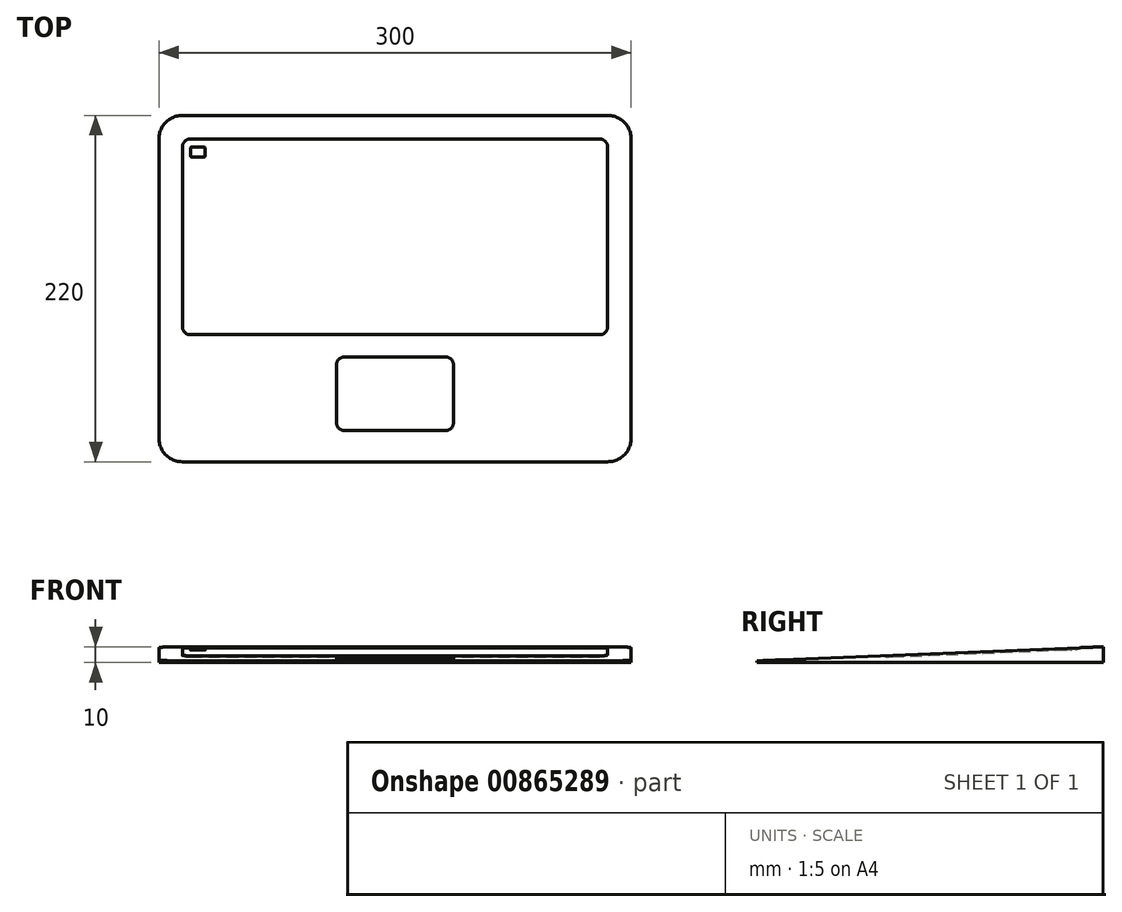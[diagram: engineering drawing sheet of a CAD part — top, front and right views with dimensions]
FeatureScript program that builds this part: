
annotation { "Feature Type Name" : "Feature", "Feature Type Description" : "" }
export const myFeature = defineFeature(function(context is Context, id is Id, definition is map)
    precondition{}
    {
        {
            var Q0;
            Q0=qCreatedBy(makeId("Right.planeOp"),FACE);
            var sketch = newSketch(context, id + "F0", { "sketchPlane" : qUnion([Q0])});
            skLineSegment(sketch, "E0", {"start": v(-104.21, 0) * mm, "end": v(115.79, 0) * mm});
            skLineSegment(sketch, "E1", {"start": v(115.79, 0) * mm, "end": v(115.79, 10) * mm});
            skLineSegment(sketch, "E2", {"start": v(115.79, 10) * mm, "end": v(-104.21, 1) * mm});
            skLineSegment(sketch, "E3", {"start": v(-104.21, 1) * mm, "end": v(-104.21, 0) * mm});
            skSolve(sketch);
        }
        {
            var Q0;
            Q0=makeQuery(id+"F0.imprint","IMPRINT",FACE,{"disambiguationData":[TD([[makeQuery(id+"F0.imprint","IMPRINT",EDGE,{"derivedFrom":sQuery(id+"F0.wireOp",EDGE,"E0")}),1.0]])]});
            extrude(context, id + "F1", {"entities" : qUnion([Q0]), "depth" : 300 * mm, "offsetDistance" : 25 * mm});
        }
        {
            var Q0;
            Q0=makeQuery(id+"F1.opExtrude","CAP_EDGE",EDGE,{"disambiguationData":[OSD([sQuery(id+"F0.wireOp",EDGE,"E1")])],"isStart":false});
            var Q1;
            Q1=makeQuery(id+"F1.opExtrude","CAP_EDGE",EDGE,{"disambiguationData":[OSD([sQuery(id+"F0.wireOp",EDGE,"E1")])],"isStart":true});
            var Q2;
            Q2=makeQuery(id+"F1.opExtrude","CAP_EDGE",EDGE,{"disambiguationData":[OSD([sQuery(id+"F0.wireOp",EDGE,"E3")])],"isStart":true});
            var Q3;
            Q3=makeQuery(id+"F1.opExtrude","CAP_EDGE",EDGE,{"disambiguationData":[OSD([sQuery(id+"F0.wireOp",EDGE,"E3")])],"isStart":false});
            fillet(context, id + "F2", {"entities" : qUnion([Q0, Q1, Q2, Q3]), "radius" : 15 * mm, "tangentPropagation" : true, "allowEdgeOverflow" : false});
        }
        {
            var Q0;
            Q0=makeQuery(id+"F1.opExtrude","SWEPT_FACE",FACE,{"disambiguationData":[OSD([sQuery(id+"F0.wireOp",EDGE,"E2")])]});
            var sketch = newSketch(context, id + "F3", { "sketchPlane" : qUnion([Q0])});
            skPoint(sketch, "E4.oppositeSnap0", {"position": v(285, 86.08) * mm});
            skLineSegment(sketch, "E4.bottom", {"start": v(20, 101.09) * mm, "end": v(280, 101.09) * mm});
            skLineSegment(sketch, "E4.top", {"start": v(20, -23.33) * mm, "end": v(280, -23.33) * mm});
            skLineSegment(sketch, "E4.left", {"start": v(15, 96.09) * mm, "end": v(15, -18.33) * mm});
            skLineSegment(sketch, "E4.right", {"start": v(285, 96.09) * mm, "end": v(285, -18.33) * mm});
            skPoint(sketch, "E5.visualSharp", {"position": v(15, 101.09) * mm});
            skArc(sketch, "E5.filletArc", {"start": v(20, 101.09) * mm, "mid": v(16.46, 99.62) * mm, "end": v(15, 96.09) * mm});
            skPoint(sketch, "E6.visualSharp", {"position": v(285, 101.09) * mm});
            skArc(sketch, "E6.filletArc", {"start": v(285, 96.09) * mm, "mid": v(283.54, 99.62) * mm, "end": v(280, 101.09) * mm});
            skPoint(sketch, "E7.visualSharp", {"position": v(285, -23.33) * mm});
            skArc(sketch, "E7.filletArc", {"start": v(280, -23.33) * mm, "mid": v(283.54, -21.86) * mm, "end": v(285, -18.33) * mm});
            skPoint(sketch, "E8.visualSharp", {"position": v(15, -23.33) * mm});
            skArc(sketch, "E8.filletArc", {"start": v(15, -18.33) * mm, "mid": v(16.46, -21.86) * mm, "end": v(20, -23.33) * mm});
            skSolve(sketch);
        }
        {
            var Q0;
            Q0=makeQuery(id+"F3.imprint","IMPRINT",FACE,{"disambiguationData":[TD([[makeQuery(id+"F3.imprint","IMPRINT",EDGE,{"derivedFrom":sQuery(id+"F3.wireOp",EDGE,"E4.bottom")}),-1.0]])]});
            extrude(context, id + "F4", {"entities" : qUnion([Q0]), "operationType" : NewBodyOperationType.REMOVE, "oppositeDirection" : true, "depth" : 1 * mm, "offsetDistance" : 25 * mm});
        }
        {
            var Q0;
            Q0=makeQuery(id+"F4.boolean.opBoolean","COPY",FACE,{"derivedFrom":makeQuery(id+"F4.opExtrude","CAP_FACE",FACE,{"disambiguationData":[OSD([sQuery(id+"F3.wireOp",EDGE,"E4.bottom"),sQuery(id+"F3.wireOp",EDGE,"E4.top"),sQuery(id+"F3.wireOp",EDGE,"E4.left"),sQuery(id+"F3.wireOp",EDGE,"E4.right")])],"isStart":false})});
            fillet(context, id + "F5", {"entities" : qUnion([Q0]), "radius" : 5 * mm, "tangentPropagation" : true, "allowEdgeOverflow" : false});
        }
        {
            var Q0;
            Q0=makeQuery(id+"F1.opExtrude","SWEPT_FACE",FACE,{"disambiguationData":[OSD([sQuery(id+"F0.wireOp",EDGE,"E2")])]});
            var sketch = newSketch(context, id + "F6", { "sketchPlane" : qUnion([Q0])});
            skLineSegment(sketch, "E9.bottom", {"start": v(117.9, -37.42) * mm, "end": v(182.1, -37.42) * mm});
            skLineSegment(sketch, "E9.top", {"start": v(117.9, -84.3) * mm, "end": v(182.1, -84.3) * mm});
            skLineSegment(sketch, "E9.left", {"start": v(112.9, -42.42) * mm, "end": v(112.9, -79.3) * mm});
            skLineSegment(sketch, "E9.right", {"start": v(187.1, -42.42) * mm, "end": v(187.1, -79.3) * mm});
            skPoint(sketch, "E9.middle", {"position": v(150, -60.85) * mm});
            skPoint(sketch, "E9.middle.positionSnap0", {"position": v(150, -23.33) * mm});
            skPoint(sketch, "E9.centerSnap0", {"position": v(150, -23.33) * mm});
            skPoint(sketch, "E10.visualSharp", {"position": v(112.9, -37.42) * mm});
            skArc(sketch, "E10.filletArc", {"start": v(117.9, -37.42) * mm, "mid": v(114.37, -38.88) * mm, "end": v(112.9, -42.42) * mm});
            skPoint(sketch, "E11.visualSharp", {"position": v(187.1, -37.42) * mm});
            skArc(sketch, "E11.filletArc", {"start": v(187.1, -42.42) * mm, "mid": v(185.63, -38.88) * mm, "end": v(182.1, -37.42) * mm});
            skPoint(sketch, "E12.visualSharp", {"position": v(187.1, -84.3) * mm});
            skArc(sketch, "E12.filletArc", {"start": v(182.1, -84.3) * mm, "mid": v(185.63, -82.83) * mm, "end": v(187.1, -79.3) * mm});
            skPoint(sketch, "E13.visualSharp", {"position": v(112.9, -84.3) * mm});
            skArc(sketch, "E13.filletArc", {"start": v(112.9, -79.3) * mm, "mid": v(114.37, -82.83) * mm, "end": v(117.9, -84.3) * mm});
            skSolve(sketch);
        }
        {
            var Q0;
            Q0=makeQuery(id+"F6.imprint","IMPRINT",FACE,{"disambiguationData":[TD([[makeQuery(id+"F6.imprint","IMPRINT",EDGE,{"derivedFrom":sQuery(id+"F6.wireOp",EDGE,"E9.bottom")}),-1.0]])]});
            extrude(context, id + "F7", {"entities" : qUnion([Q0]), "operationType" : NewBodyOperationType.REMOVE, "oppositeDirection" : true, "depth" : 0.1 * mm, "offsetDistance" : 25 * mm});
        }
        {
            var Q0;
            Q0=makeQuery(id+"F4.boolean.opBoolean","COPY",FACE,{"derivedFrom":makeQuery(id+"F4.opExtrude","CAP_FACE",FACE,{"disambiguationData":[OSD([sQuery(id+"F3.wireOp",EDGE,"E4.bottom"),sQuery(id+"F3.wireOp",EDGE,"E4.top"),sQuery(id+"F3.wireOp",EDGE,"E4.left"),sQuery(id+"F3.wireOp",EDGE,"E4.right"),sQuery(id+"F3.wireOp",EDGE,"E5.filletArc"),sQuery(id+"F3.wireOp",EDGE,"E6.filletArc"),sQuery(id+"F3.wireOp",EDGE,"E7.filletArc"),sQuery(id+"F3.wireOp",EDGE,"E8.filletArc")])],"isStart":false})});
            var sketch = newSketch(context, id + "F8", { "sketchPlane" : qUnion([Q0])});
            skLineSegment(sketch, "E14.bottom", {"start": v(21, 96.09) * mm, "end": v(28.5, 96.09) * mm});
            skLineSegment(sketch, "E14.top", {"start": v(21, 89.47) * mm, "end": v(28.5, 89.47) * mm});
            skLineSegment(sketch, "E14.left", {"start": v(20, 95.09) * mm, "end": v(20, 90.47) * mm});
            skLineSegment(sketch, "E14.right", {"start": v(29.5, 95.09) * mm, "end": v(29.5, 90.47) * mm});
            skPoint(sketch, "E15.visualSharp", {"position": v(20, 96.09) * mm});
            skArc(sketch, "E15.filletArc", {"start": v(21, 96.09) * mm, "mid": v(20.3, 95.8) * mm, "end": v(20, 95.09) * mm});
            skPoint(sketch, "E16.visualSharp", {"position": v(29.5, 96.09) * mm});
            skArc(sketch, "E16.filletArc", {"start": v(29.5, 95.09) * mm, "mid": v(29.21, 95.8) * mm, "end": v(28.5, 96.09) * mm});
            skPoint(sketch, "E17.visualSharp", {"position": v(29.5, 89.47) * mm});
            skArc(sketch, "E17.filletArc", {"start": v(28.5, 89.47) * mm, "mid": v(29.21, 89.77) * mm, "end": v(29.5, 90.47) * mm});
            skPoint(sketch, "E18.visualSharp", {"position": v(20, 89.47) * mm});
            skArc(sketch, "E18.filletArc", {"start": v(20, 90.47) * mm, "mid": v(20.3, 89.77) * mm, "end": v(21, 89.47) * mm});
            skSolve(sketch);
        }
        {
            var Q0;
            Q0=makeQuery(id+"F8.imprint","IMPRINT",FACE,{"disambiguationData":[TD([[makeQuery(id+"F8.imprint","IMPRINT",EDGE,{"derivedFrom":sQuery(id+"F8.wireOp",EDGE,"E14.bottom")}),-1.0]])]});
            extrude(context, id + "F9", {"entities" : qUnion([Q0]), "operationType" : NewBodyOperationType.REMOVE, "oppositeDirection" : true, "depth" : 0.1 * mm, "offsetDistance" : 25 * mm});
        }
    });
